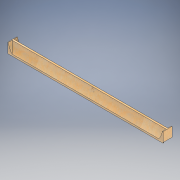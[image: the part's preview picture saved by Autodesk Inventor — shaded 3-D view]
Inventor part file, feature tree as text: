
AUTODESK INVENTOR PART (.ipt)
format: ipt  version: 2022.2 (Build 262287010, 287A)  size: 189,440 bytes
history: native  units: in
note: dims shown in document units (in); Inventor stores cm internally (conversion verified against a paired STEP export)
features: direct_edit x1, extrude x1, sketch x1, projected_geometry x1, other x1, revolve x1
ambient origin geometry x8: Origin, YZ Plane, XZ Plane, XY Plane, X Axis, Y Axis, Z Axis, Center Point
bodies: Solid1 (feature_tree)
feature tree (6):
  direct_edit  "Direct Edit1"
  extrude  "Extrusion1"  Depth=1.0in TaperAngle=0.0deg
  sketch  "Sketch1"  dims[d0=-1.2368in d1=1.0in d2=0.0in]
  projected_geometry  "Projected Loop1"
  other  "Transom (2)"
  revolve  "Rotate1"  [1 undecoded]
note: 1 required parameter value undecoded (feature->parameter linkage not recoverable at this tier; creation-order binding heuristic only, values carry confidence <= 0.55)
